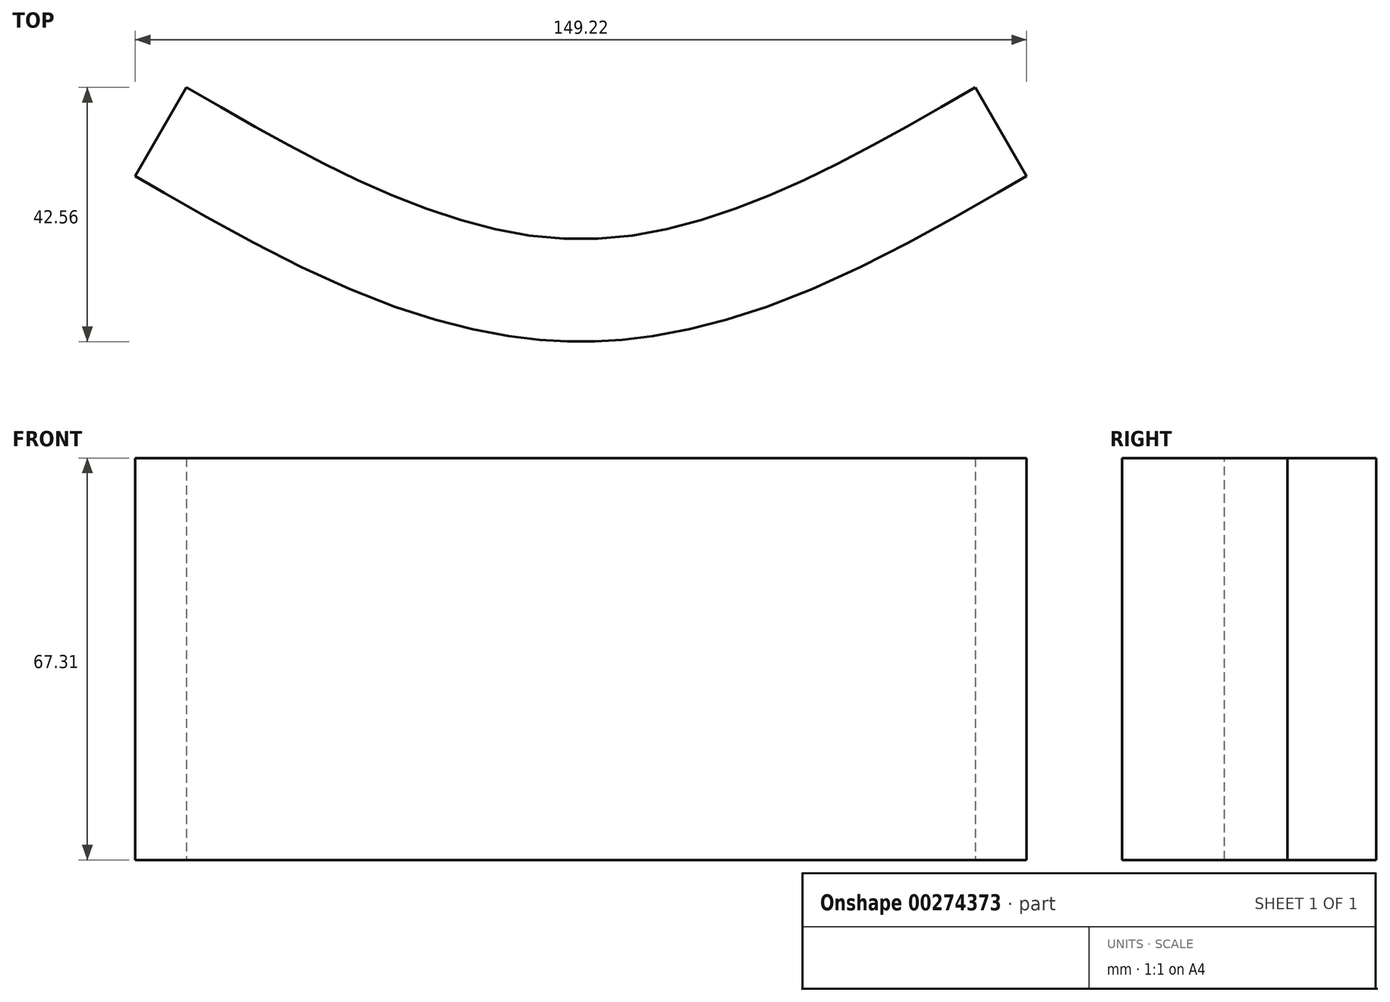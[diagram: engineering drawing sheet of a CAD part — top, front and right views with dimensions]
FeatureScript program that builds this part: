
annotation { "Feature Type Name" : "Feature", "Feature Type Description" : "" }
export const myFeature = defineFeature(function(context is Context, id is Id, definition is map)
    precondition{}
    {
        {
            var Q0;
            Q0=qCreatedBy(makeId("Top.planeOp"),FACE);
            var sketch = newSketch(context, id + "F0", { "sketchPlane" : qUnion([Q0])});
            skFitSpline(sketch, "E0", {"points": [v(-66.04, 25.4) * mm, v(0, 0) * mm, v(66.04, 25.4) * mm], "startDerivative": vector(132.08, -76.2) * mm, "endDerivative": vector(132.08, 76.2) * mm});
            skFitSpline(sketch, "E1.0", {"points": [v(-74.6, 10.55) * mm, v(-71.86, 8.96) * mm, v(-66.29, 5.75) * mm, v(-57.72, 0.96) * mm, v(-48.93, -3.64) * mm, v(-39.88, -7.89) * mm, v(-32.07, -10.99) * mm, v(-25.64, -13.1) * mm, v(-20.72, -14.48) * mm, v(-15.7, -15.62) * mm, v(-11.42, -16.33) * mm, v(-7.95, -16.74) * mm, v(-5.33, -16.97) * mm, v(-2.68, -17.11) * mm, v(0, -17.16) * mm, v(2.68, -17.11) * mm, v(5.33, -16.97) * mm, v(7.95, -16.74) * mm, v(11.42, -16.33) * mm, v(15.7, -15.62) * mm, v(20.72, -14.48) * mm, v(25.64, -13.1) * mm, v(32.07, -10.99) * mm, v(39.88, -7.89) * mm, v(48.93, -3.64) * mm, v(57.72, 0.96) * mm, v(66.29, 5.75) * mm, v(71.86, 8.96) * mm, v(74.6, 10.55) * mm]});
            skLineSegment(sketch, "E2", {"start": v(-74.6, 10.55) * mm, "end": v(-66.04, 25.4) * mm});
            skLineSegment(sketch, "E3", {"start": v(66.04, 25.4) * mm, "end": v(74.6, 10.55) * mm});
            skSolve(sketch);
        }
        {
            var Q0;
            Q0 = qSketchRegion(id + "F0", true);
            extrude(context, id + "F1", {"entities" : qUnion([Q0]), "depth" : 67.3 * mm});
        }
    });
